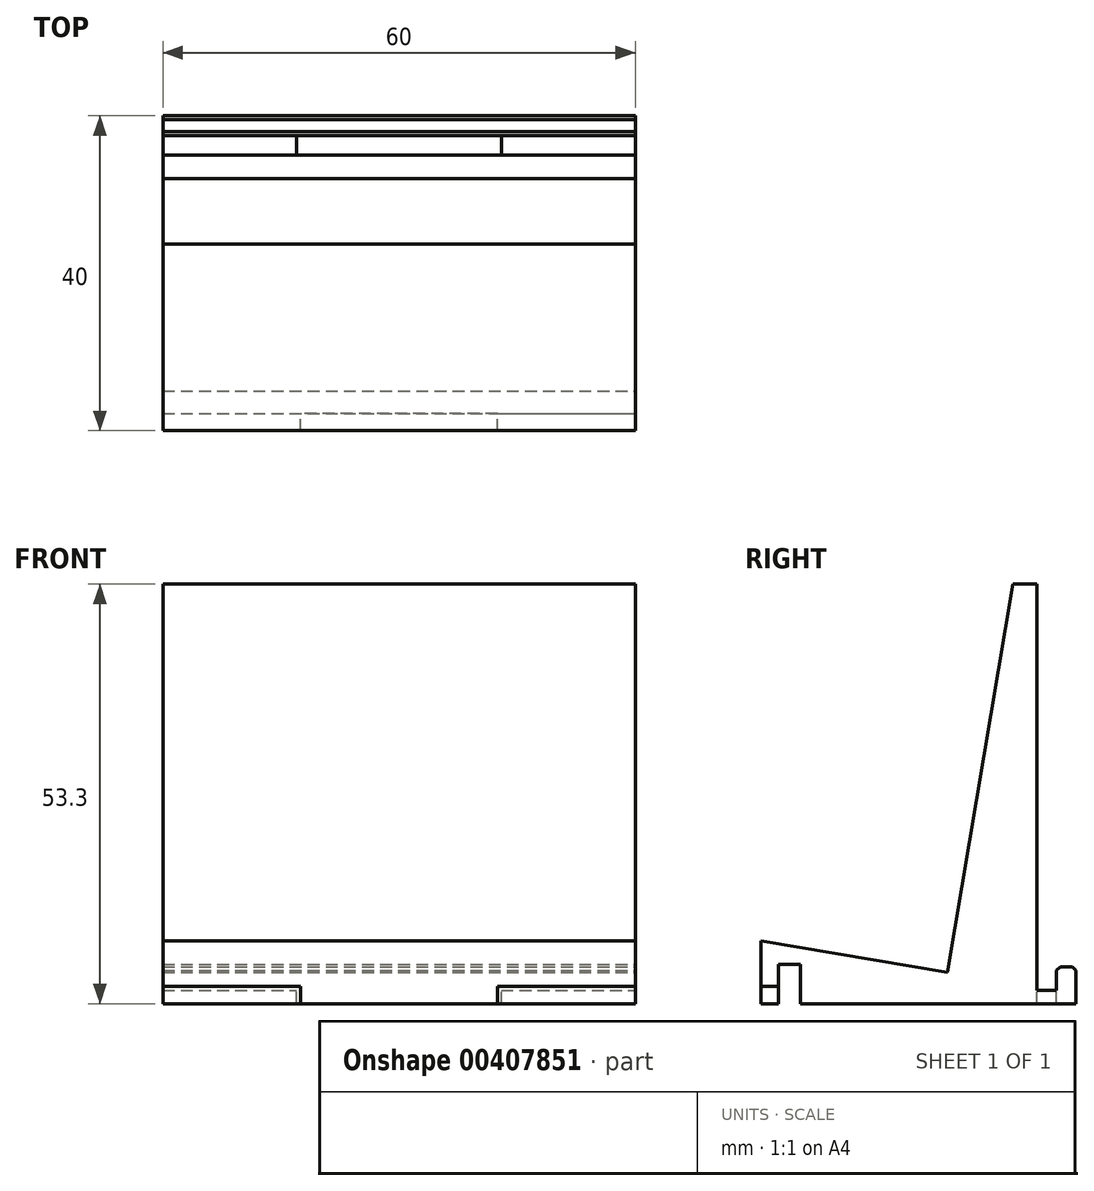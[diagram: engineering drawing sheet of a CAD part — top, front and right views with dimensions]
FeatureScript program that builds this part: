
annotation { "Feature Type Name" : "Feature", "Feature Type Description" : "" }
export const myFeature = defineFeature(function(context is Context, id is Id, definition is map)
    precondition{}
    {
        {
            var Q0;
            Q0=qCreatedBy(makeId("Top.planeOp"),FACE);
            var sketch = newSketch(context, id + "F0", { "sketchPlane" : qUnion([Q0])});
            skLineSegment(sketch, "E0.bottom", {"start": v(-30, 20) * mm, "end": v(30, 20) * mm});
            skLineSegment(sketch, "E0.top", {"start": v(-30, -20) * mm, "end": v(30, -20) * mm});
            skLineSegment(sketch, "E0.left", {"start": v(-30, 20) * mm, "end": v(-30, -20) * mm});
            skLineSegment(sketch, "E0.right", {"start": v(30, 20) * mm, "end": v(30, -20) * mm});
            skPoint(sketch, "E1", {"position": v(0, 20) * mm});
            skPoint(sketch, "E2", {"position": v(-30, 0) * mm});
            skSolve(sketch);
        }
        {
            var Q0;
            Q0=makeQuery(id+"F0.imprint","IMPRINT",FACE,{"disambiguationData":[TD([[makeQuery(id+"F0.imprint","IMPRINT",EDGE,{"derivedFrom":sQuery(id+"F0.wireOp",EDGE,"E0.bottom")}),-1.0]])]});
            extrude(context, id + "F1", {"entities" : qUnion([Q0]), "depth" : 4 * mm});
        }
        {
            var Q0;
            Q0=makeQuery(id+"F1.opExtrude","SWEPT_FACE",FACE,{"disambiguationData":[OSD([sQuery(id+"F0.wireOp",EDGE,"E0.right")])]});
            var sketch = newSketch(context, id + "F2", { "sketchPlane" : qUnion([Q0])});
            skLineSegment(sketch, "E3", {"start": v(-20, 4) * mm, "end": v(-20, 8) * mm});
            skLineSegment(sketch, "E4", {"start": v(-20, 8) * mm, "end": v(3.67, 4) * mm});
            skLineSegment(sketch, "E5", {"start": v(3.67, 4) * mm, "end": v(12, 53.3) * mm});
            skLineSegment(sketch, "E6", {"start": v(12, 53.3) * mm, "end": v(15, 53.3) * mm});
            skLineSegment(sketch, "E7", {"start": v(15, 53.3) * mm, "end": v(15, 4) * mm});
            skSolve(sketch);
        }
        {
            var Q0;
            {var subQ0=sQuery(id+"F2.wireOp",EDGE,"E5");Q0=makeQuery(id+"F2.imprint","IMPRINT",FACE,{"disambiguationData":[TD([[makeQuery(id+"F2.imprint","IMPRINT",EDGE,{"derivedFrom":subQ0}),-1.0]])]});}
            var Q1;
            {var subQ0=sQuery(id+"F2.wireOp",EDGE,"E3");Q1=makeQuery(id+"F2.imprint","IMPRINT",FACE,{"disambiguationData":[TD([[makeQuery(id+"F2.imprint","IMPRINT",EDGE,{"derivedFrom":subQ0}),-1.0]])]});}
            var Q2;
            Q2=makeQuery(id+"F1.opExtrude","SWEPT_FACE",FACE,{"disambiguationData":[OSD([sQuery(id+"F0.wireOp",EDGE,"E0.left")])]});
            extrude(context, id + "F3", {"entities" : qUnion([Q0, Q1]), "operationType" : NewBodyOperationType.ADD, "endBound" : BoundingType.UP_TO_SURFACE, "oppositeDirection" : true, "endBoundEntityFace" : qUnion([Q2]), "depth" : 25 * mm});
        }
        {
            var Q0;
            {var subQ0=sQuery(id+"F0.wireOp",EDGE,"E0.right");Q0=makeQuery(id+"F3.boolean.opBoolean","MERGE",FACE,{"derivedFrom":[makeQuery(id+"F1.opExtrude","SWEPT_FACE",FACE,{"disambiguationData":[OSD([subQ0])]}),makeQuery(id+"F3.opExtrude","CAP_FACE",FACE,{"disambiguationData":[OSD([subQ0,sQuery(id+"F2.wireOp",EDGE,"E3"),sQuery(id+"F2.wireOp",EDGE,"E4")])],"isStart":true}),makeQuery(id+"F3.opExtrude","CAP_FACE",FACE,{"disambiguationData":[OSD([subQ0,sQuery(id+"F2.wireOp",EDGE,"E5"),sQuery(id+"F2.wireOp",EDGE,"E6"),sQuery(id+"F2.wireOp",EDGE,"E7")])],"isStart":true})]});}
            var sketch = newSketch(context, id + "F4", { "sketchPlane" : qUnion([Q0])});
            skLineSegment(sketch, "E8.bottom", {"start": v(-17.8, 0) * mm, "end": v(-15, 0) * mm});
            skLineSegment(sketch, "E8.top", {"start": v(-17.8, 5) * mm, "end": v(-15, 5) * mm});
            skLineSegment(sketch, "E8.left", {"start": v(-17.8, 0) * mm, "end": v(-17.8, 5) * mm});
            skLineSegment(sketch, "E8.right", {"start": v(-15, 0) * mm, "end": v(-15, 5) * mm});
            skLineSegment(sketch, "E9.bottom", {"start": v(20, 4) * mm, "end": v(17.5, 4) * mm});
            skLineSegment(sketch, "E9.top", {"start": v(20, 4.7) * mm, "end": v(17.5, 4.7) * mm});
            skLineSegment(sketch, "E9.left", {"start": v(20, 4) * mm, "end": v(20, 4.7) * mm});
            skLineSegment(sketch, "E9.right", {"start": v(17.5, 4) * mm, "end": v(17.5, 4.7) * mm});
            skLineSegment(sketch, "E10.bottom", {"start": v(17.5, 4) * mm, "end": v(15, 4) * mm});
            skLineSegment(sketch, "E10.top", {"start": v(17.5, 1.7) * mm, "end": v(15, 1.7) * mm});
            skLineSegment(sketch, "E10.left", {"start": v(17.5, 4) * mm, "end": v(17.5, 1.7) * mm});
            skLineSegment(sketch, "E10.right", {"start": v(15, 4) * mm, "end": v(15, 1.7) * mm});
            skLineSegment(sketch, "E11.bottom", {"start": v(-17.8, 0) * mm, "end": v(-20, 0) * mm});
            skLineSegment(sketch, "E11.top", {"start": v(-17.8, 2.2) * mm, "end": v(-20, 2.2) * mm});
            skLineSegment(sketch, "E11.left", {"start": v(-17.8, 0) * mm, "end": v(-17.8, 2.2) * mm});
            skLineSegment(sketch, "E11.right", {"start": v(-20, 0) * mm, "end": v(-20, 2.2) * mm});
            skSolve(sketch);
        }
        {
            var Q0;
            Q0=makeQuery(id+"F4.imprint","IMPRINT",FACE,{"disambiguationData":[TD([[makeQuery(id+"F4.imprint","IMPRINT",EDGE,{"derivedFrom":sQuery(id+"F4.wireOp",EDGE,"E11.bottom")}),-1.0]])]});
            var Q1;
            Q1=makeQuery(id+"F4.imprint","IMPRINT",FACE,{"disambiguationData":[TD([[makeQuery(id+"F4.imprint","IMPRINT",EDGE,{"derivedFrom":sQuery(id+"F4.wireOp",EDGE,"E8.bottom")}),-1.0]])]});
            var Q2;
            Q2=makeQuery(id+"F4.imprint","IMPRINT",FACE,{"disambiguationData":[TD([[makeQuery(id+"F4.imprint","IMPRINT",EDGE,{"derivedFrom":sQuery(id+"F4.wireOp",EDGE,"E10.bottom")}),1.0]])]});
            extrude(context, id + "F5", {"entities" : qUnion([Q0, Q1, Q2]), "operationType" : NewBodyOperationType.REMOVE, "endBound" : BoundingType.UP_TO_NEXT, "oppositeDirection" : true, "depth" : 25 * mm});
        }
        {
            var Q0;
            Q0=makeQuery(id+"F4.imprint","IMPRINT",FACE,{"disambiguationData":[TD([[makeQuery(id+"F4.imprint","IMPRINT",EDGE,{"derivedFrom":sQuery(id+"F4.wireOp",EDGE,"E9.bottom")}),-1.0]])]});
            var Q1;
            {var subQ0=sQuery(id+"F0.wireOp",EDGE,"E0.left");Q1=makeQuery(id+"F3.boolean.opBoolean","MERGE",FACE,{"derivedFrom":[makeQuery(id+"F1.opExtrude","SWEPT_FACE",FACE,{"disambiguationData":[OSD([subQ0])]}),makeQuery(id+"F3.opExtrude","CAP_FACE",FACE,{"disambiguationData":[OSD([subQ0]),ownerDisambiguation([makeQuery(id+"F2.imprint","IMPRINT",EDGE,{"derivedFrom":sQuery(id+"F2.wireOp",EDGE,"E3")})])],"isStart":false}),makeQuery(id+"F3.opExtrude","CAP_FACE",FACE,{"disambiguationData":[OSD([subQ0]),ownerDisambiguation([makeQuery(id+"F2.imprint","IMPRINT",EDGE,{"derivedFrom":sQuery(id+"F2.wireOp",EDGE,"E5")})])],"isStart":false})]});}
            extrude(context, id + "F6", {"entities" : qUnion([Q0]), "operationType" : NewBodyOperationType.ADD, "endBound" : BoundingType.UP_TO_SURFACE, "oppositeDirection" : true, "endBoundEntityFace" : qUnion([Q1]), "depth" : 25 * mm});
        }
        {
            var Q0;
            Q0=makeQuery(id+"F5.boolean.opBoolean","COPY",FACE,{"derivedFrom":makeQuery(id+"F5.opExtrude","SWEPT_FACE",FACE,{"disambiguationData":[OSD([sQuery(id+"F4.wireOp",EDGE,"E11.top")])]})});
            var sketch = newSketch(context, id + "F7", { "sketchPlane" : qUnion([Q0])});
            skLineSegment(sketch, "E12.bottom", {"start": v(-12.5, 20) * mm, "end": v(12.5, 20) * mm});
            skLineSegment(sketch, "E12.top", {"start": v(-12.5, 17.8) * mm, "end": v(12.5, 17.8) * mm});
            skLineSegment(sketch, "E12.left", {"start": v(-12.5, 20) * mm, "end": v(-12.5, 17.8) * mm});
            skLineSegment(sketch, "E12.right", {"start": v(12.5, 20) * mm, "end": v(12.5, 17.8) * mm});
            skPoint(sketch, "E13", {"position": v(0, 20) * mm});
            skSolve(sketch);
        }
        {
            var Q0;
            Q0=makeQuery(id+"F7.imprint","IMPRINT",FACE,{"disambiguationData":[TD([[makeQuery(id+"F7.imprint","IMPRINT",EDGE,{"derivedFrom":sQuery(id+"F7.wireOp",EDGE,"E12.bottom")}),-1.0]])]});
            var Q1;
            Q1=makeQuery(id+"F1.opExtrude","CAP_FACE",FACE,{"disambiguationData":[OSD([sQuery(id+"F0.wireOp",EDGE,"E0.bottom"),sQuery(id+"F0.wireOp",EDGE,"E0.top"),sQuery(id+"F0.wireOp",EDGE,"E0.left"),sQuery(id+"F0.wireOp",EDGE,"E0.right")])],"isStart":true});
            extrude(context, id + "F8", {"entities" : qUnion([Q0]), "operationType" : NewBodyOperationType.ADD, "endBound" : BoundingType.UP_TO_SURFACE, "endBoundEntityFace" : qUnion([Q1]), "depth" : 25 * mm});
        }
        {
            var Q0;
            Q0=makeQuery(id+"F5.boolean.opBoolean","COPY",FACE,{"derivedFrom":makeQuery(id+"F5.opExtrude","SWEPT_FACE",FACE,{"disambiguationData":[OSD([sQuery(id+"F4.wireOp",EDGE,"E10.top")])]})});
            var sketch = newSketch(context, id + "F9", { "sketchPlane" : qUnion([Q0])});
            skLineSegment(sketch, "E14.bottom", {"start": v(13, 15) * mm, "end": v(-13, 15) * mm});
            skLineSegment(sketch, "E14.top", {"start": v(13, 17.5) * mm, "end": v(-13, 17.5) * mm});
            skLineSegment(sketch, "E14.left", {"start": v(13, 15) * mm, "end": v(13, 17.5) * mm});
            skLineSegment(sketch, "E14.right", {"start": v(-13, 15) * mm, "end": v(-13, 17.5) * mm});
            skPoint(sketch, "E15", {"position": v(0, 15) * mm});
            skSolve(sketch);
        }
        {
            var Q0;
            Q0=makeQuery(id+"F9.imprint","IMPRINT",FACE,{"disambiguationData":[TD([[makeQuery(id+"F9.imprint","IMPRINT",EDGE,{"derivedFrom":sQuery(id+"F9.wireOp",EDGE,"E14.bottom")}),1.0]])]});
            extrude(context, id + "F10", {"entities" : qUnion([Q0]), "operationType" : NewBodyOperationType.REMOVE, "endBound" : BoundingType.UP_TO_NEXT, "oppositeDirection" : true, "depth" : 25 * mm});
        }
        {
            var Q0;
            Q0=makeQuery(id+"F6.opExtrude","SWEPT_EDGE",EDGE,{"disambiguationData":[OSD([sQuery(id+"F4.wireOp",EDGE,"E9.top"),sQuery(id+"F4.wireOp",EDGE,"E9.left")])]});
            var Q1;
            Q1=makeQuery(id+"F6.opExtrude","SWEPT_EDGE",EDGE,{"disambiguationData":[OSD([sQuery(id+"F4.wireOp",EDGE,"E9.top"),sQuery(id+"F4.wireOp",EDGE,"E9.right")])]});
            var Q2;
            Q2=makeQuery(id+"F10.boolean.opBoolean","COPY",EDGE,{"derivedFrom":makeQuery(id+"F10.opExtrude","CAP_EDGE",EDGE,{"disambiguationData":[OSD([sQuery(id+"F9.wireOp",EDGE,"E14.right")])],"isStart":true})});
            var Q3;
            Q3=makeQuery(id+"F10.boolean.opBoolean","COPY",EDGE,{"derivedFrom":makeQuery(id+"F10.opExtrude","CAP_EDGE",EDGE,{"disambiguationData":[OSD([sQuery(id+"F9.wireOp",EDGE,"E14.left")])],"isStart":true})});
            chamfer(context, id + "F11", {"entities" : qUnion([Q0, Q1, Q2, Q3]), "width" : 0.5 * mm, "tangentPropagation" : true});
        }
    });
